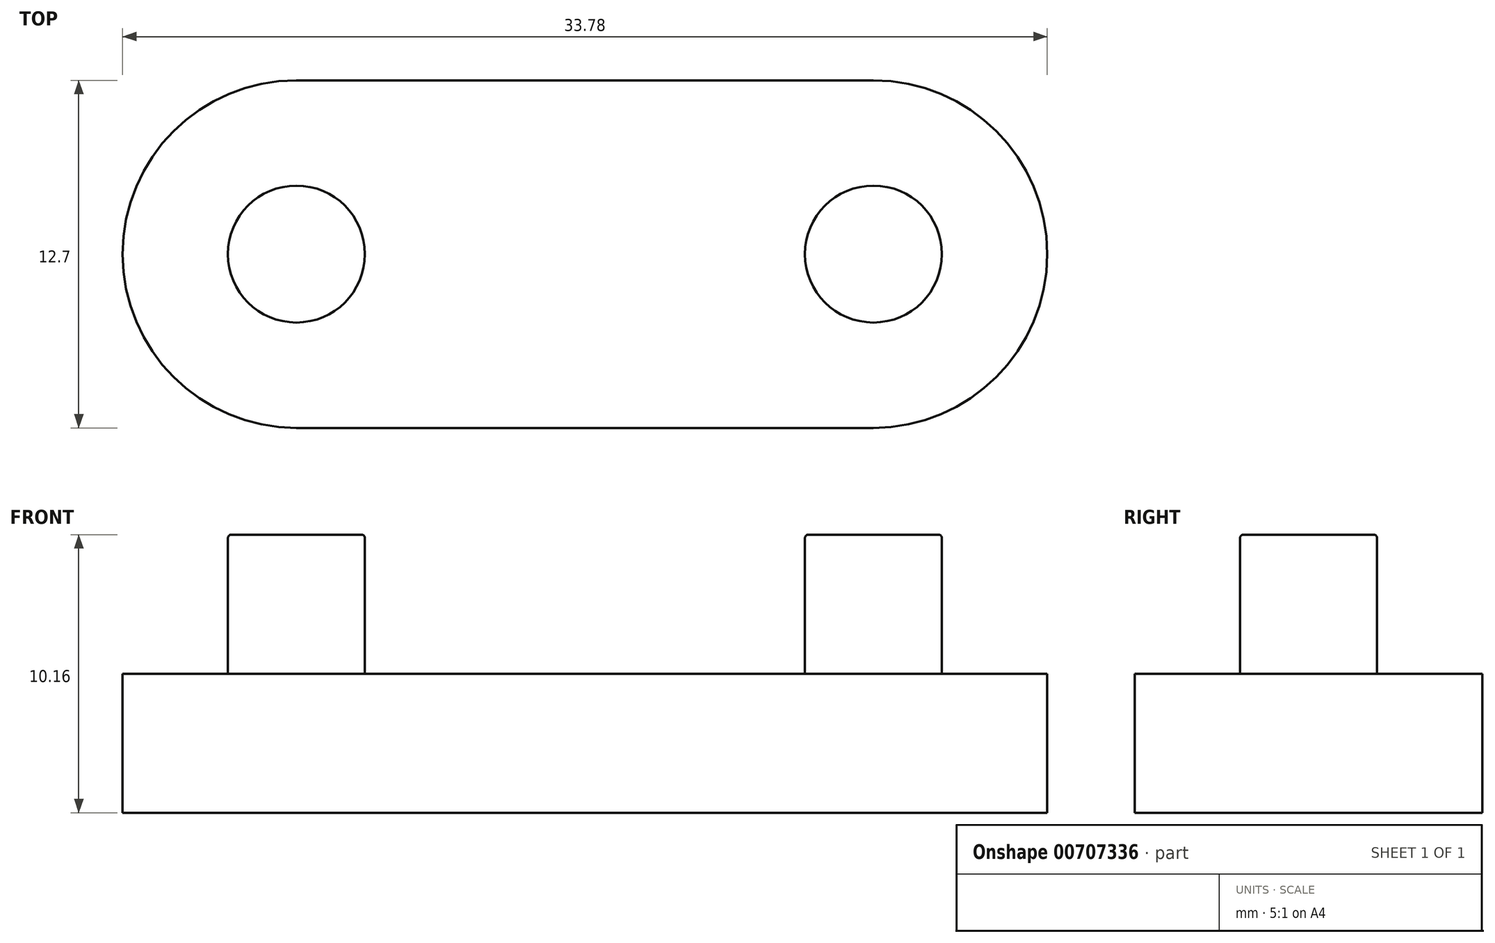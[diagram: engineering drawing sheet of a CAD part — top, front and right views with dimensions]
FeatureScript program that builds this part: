
annotation { "Feature Type Name" : "Feature", "Feature Type Description" : "" }
export const myFeature = defineFeature(function(context is Context, id is Id, definition is map)
    precondition{}
    {
        {
            var Q0;
            Q0=qCreatedBy(makeId("Top.planeOp"),FACE);
            var sketch = newSketch(context, id + "F0", { "sketchPlane" : qUnion([Q0])});
            skLineSegment(sketch, "E0.bottom", {"start": v(-10.54, 6.35) * mm, "end": v(10.54, 6.35) * mm});
            skLineSegment(sketch, "E0.top", {"start": v(-10.54, -6.35) * mm, "end": v(10.54, -6.35) * mm});
            skLineSegment(sketch, "E0.left", {"start": v(-10.54, 6.35) * mm, "end": v(-10.54, -6.35) * mm});
            skLineSegment(sketch, "E0.right", {"start": v(10.54, 6.35) * mm, "end": v(10.54, -6.35) * mm});
            skPoint(sketch, "E0.middle", {"position": v(0, 0) * mm});
            skArc(sketch, "E1", {"start": v(10.54, 6.35) * mm, "mid": v(16.9, 0) * mm, "end": v(10.54, -6.35) * mm});
            skArc(sketch, "E2", {"start": v(-10.54, 6.35) * mm, "mid": v(-16.9, 0) * mm, "end": v(-10.54, -6.35) * mm});
            skSolve(sketch);
        }
        {
            var Q0;
            Q0 = qSketchRegion(id + "F0", true);
            extrude(context, id + "F1", {"entities" : qUnion([Q0]), "depth" : 5.08 * mm, "offsetDistance" : 25.4 * mm});
        }
        {
            var Q0;
            Q0=makeQuery(id+"F1.opExtrude","CAP_FACE",FACE,{"disambiguationData":[OSD([sQuery(id+"F0.wireOp",EDGE,"E0.bottom"),sQuery(id+"F0.wireOp",EDGE,"E0.top"),sQuery(id+"F0.wireOp",EDGE,"E1"),sQuery(id+"F0.wireOp",EDGE,"E2")])],"isStart":false});
            var sketch = newSketch(context, id + "F2", { "sketchPlane" : qUnion([Q0])});
            skCircle(sketch, "E3", {"center": v(-10.54, 0) * mm, "radius": 2.5 * mm});
            skCircle(sketch, "E4", {"center": v(10.54, 0) * mm, "radius": 2.5 * mm});
            skSolve(sketch);
        }
        {
            var Q0;
            Q0=makeQuery(id+"F2.imprint","IMPRINT",FACE,{"disambiguationData":[TD([[makeQuery(id+"F2.imprint","IMPRINT",EDGE,{"derivedFrom":sQuery(id+"F2.wireOp",EDGE,"E3")}),1.0]])]});
            var Q1;
            Q1=makeQuery(id+"F2.imprint","IMPRINT",FACE,{"disambiguationData":[TD([[makeQuery(id+"F2.imprint","IMPRINT",EDGE,{"derivedFrom":sQuery(id+"F2.wireOp",EDGE,"E4")}),1.0]])]});
            extrude(context, id + "F3", {"entities" : qUnion([Q0, Q1]), "operationType" : NewBodyOperationType.ADD, "depth" : 5.08 * mm, "offsetDistance" : 25.4 * mm});
        }
        {
            var Q0;
            Q0=makeQuery(id+"F3.opExtrude","CAP_FACE",FACE,{"disambiguationData":[OSD([sQuery(id+"F2.wireOp",EDGE,"E3")])],"isStart":false});
            var Q1;
            Q1=makeQuery(id+"F3.opExtrude","CAP_FACE",FACE,{"disambiguationData":[OSD([sQuery(id+"F2.wireOp",EDGE,"E4")])],"isStart":false});
            fillet(context, id + "F4", {"entities" : qUnion([Q0, Q1]), "radius" : 0.13 * mm, "tangentPropagation" : true, "allowEdgeOverflow" : false});
        }
    });
